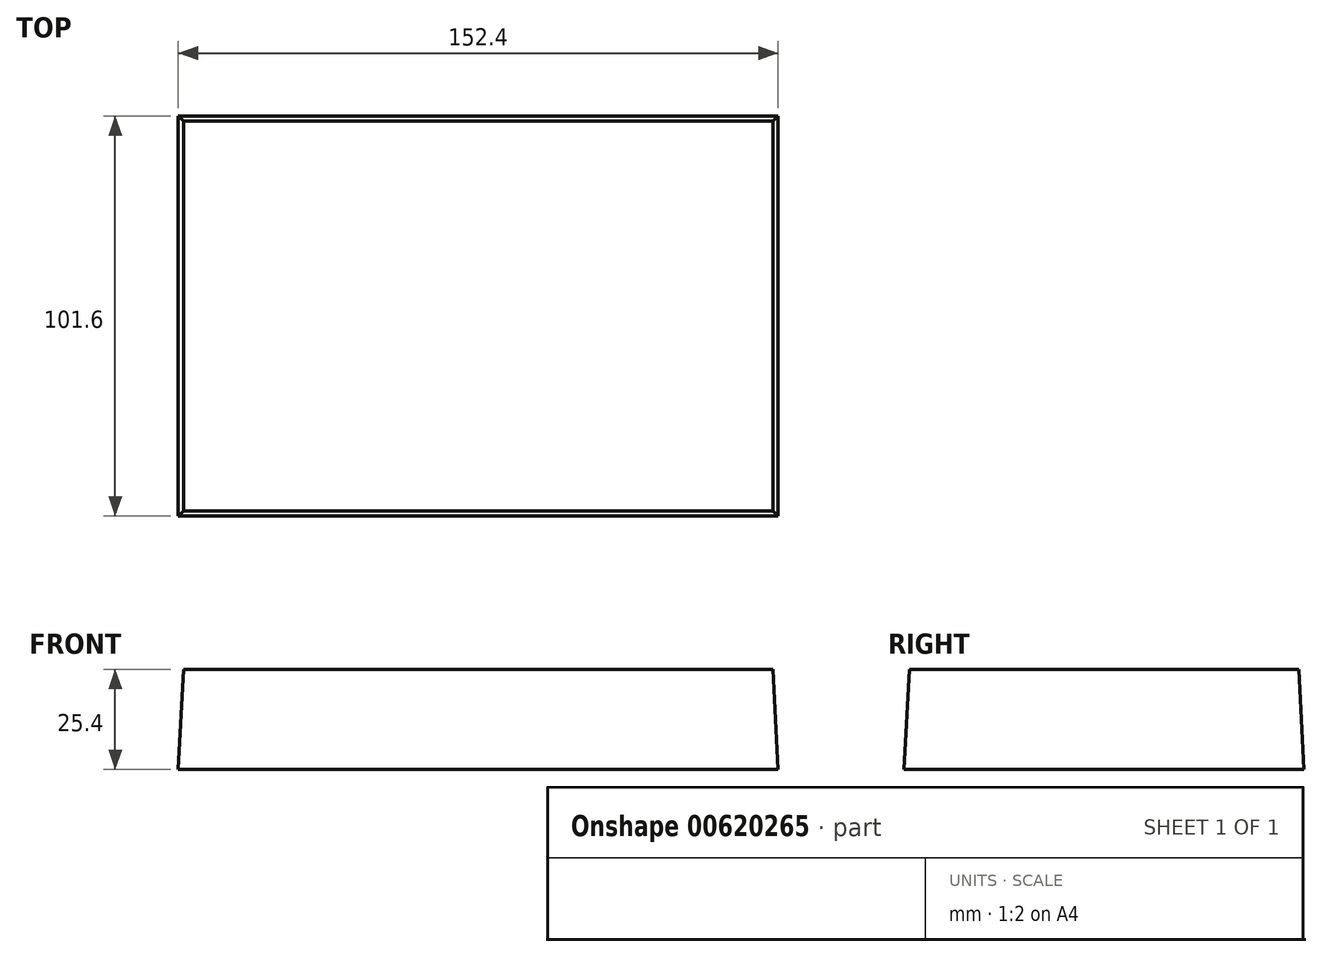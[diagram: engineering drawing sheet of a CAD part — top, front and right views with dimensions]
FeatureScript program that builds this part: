
annotation { "Feature Type Name" : "Feature", "Feature Type Description" : "" }
export const myFeature = defineFeature(function(context is Context, id is Id, definition is map)
    precondition{}
    {
        {
            var Q0;
            Q0=qCreatedBy(makeId("Top.planeOp"),FACE);
            var sketch = newSketch(context, id + "F0", { "sketchPlane" : qUnion([Q0])});
            skLineSegment(sketch, "E0.bottom", {"start": v(76.2, 50.8) * mm, "end": v(-76.2, 50.8) * mm});
            skLineSegment(sketch, "E0.top", {"start": v(76.2, -50.8) * mm, "end": v(-76.2, -50.8) * mm});
            skLineSegment(sketch, "E0.left", {"start": v(76.2, 50.8) * mm, "end": v(76.2, -50.8) * mm});
            skLineSegment(sketch, "E0.right", {"start": v(-76.2, 50.8) * mm, "end": v(-76.2, -50.8) * mm});
            skPoint(sketch, "E0.middle", {"position": v(0, 0) * mm});
            skSolve(sketch);
        }
        {
            var Q0;
            Q0=makeQuery(id+"F0.imprint","IMPRINT",FACE,{"disambiguationData":[TD([[makeQuery(id+"F0.imprint","IMPRINT",EDGE,{"derivedFrom":sQuery(id+"F0.wireOp",EDGE,"E0.bottom")}),1.0]])]});
            extrude(context, id + "F1", {"entities" : qUnion([Q0]), "depth" : 25.4 * mm, "offsetDistance" : 25.4 * mm, "hasDraft" : true, "draftAngle" : 3 * degree, "draftPullDirection" : true});
        }
    });
